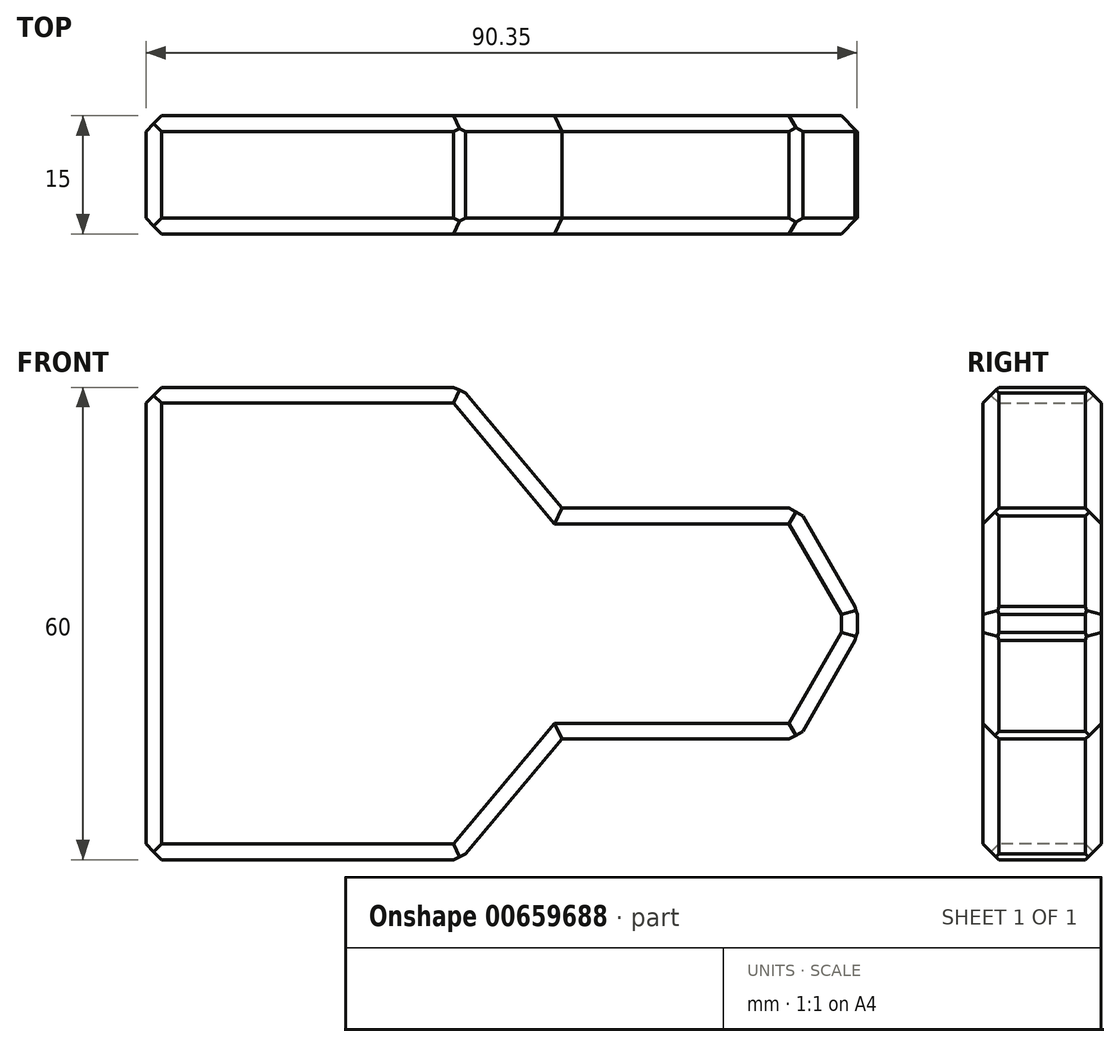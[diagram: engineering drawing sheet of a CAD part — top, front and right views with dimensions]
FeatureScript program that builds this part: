
annotation { "Feature Type Name" : "Feature", "Feature Type Description" : "" }
export const myFeature = defineFeature(function(context is Context, id is Id, definition is map)
    precondition{}
    {
        {
            var Q0;
            Q0=qCreatedBy(makeId("Front.planeOp"),FACE);
            var sketch = newSketch(context, id + "F0", { "sketchPlane" : qUnion([Q0])});
            skLineSegment(sketch, "E0", {"start": v(-70.7, 35.39) * mm, "end": v(-70.7, -24.61) * mm});
            skLineSegment(sketch, "E1", {"start": v(-70.7, -24.61) * mm, "end": v(-30.7, -24.61) * mm});
            skLineSegment(sketch, "E2", {"start": v(-30.7, -24.61) * mm, "end": v(-17.85, -9.3) * mm});
            skLineSegment(sketch, "E3", {"start": v(-17.85, -9.3) * mm, "end": v(12.15, -9.3) * mm});
            skLineSegment(sketch, "E4", {"start": v(12.15, -9.3) * mm, "end": v(19.65, 3.7) * mm});
            skLineSegment(sketch, "E5", {"start": v(-70.7, 35.39) * mm, "end": v(-30.7, 35.39) * mm});
            skLineSegment(sketch, "E6", {"start": v(-30.7, 35.39) * mm, "end": v(-17.85, 20.06) * mm});
            skLineSegment(sketch, "E7", {"start": v(-17.85, 20.06) * mm, "end": v(12.15, 20.06) * mm});
            skLineSegment(sketch, "E8", {"start": v(12.15, 20.06) * mm, "end": v(19.65, 7.07) * mm});
            skLineSegment(sketch, "E9", {"start": v(19.65, 7.07) * mm, "end": v(19.65, 3.7) * mm});
            skSolve(sketch);
        }
        {
            var Q0;
            Q0=makeQuery(id+"F0.imprint","IMPRINT",FACE,{"disambiguationData":[TD([[makeQuery(id+"F0.imprint","IMPRINT",EDGE,{"derivedFrom":sQuery(id+"F0.wireOp",EDGE,"E0")}),1.0]])]});
            extrude(context, id + "F1", {"entities" : qUnion([Q0]), "depth" : 15 * mm, "offsetDistance" : 25 * mm});
        }
        {
            var Q0;
            Q0=makeQuery(id+"F1.opExtrude","CAP_EDGE",EDGE,{"disambiguationData":[OSD([sQuery(id+"F0.wireOp",EDGE,"E5")])],"isStart":false});
            var Q1;
            Q1=makeQuery(id+"F1.opExtrude","CAP_EDGE",EDGE,{"disambiguationData":[OSD([sQuery(id+"F0.wireOp",EDGE,"E6")])],"isStart":false});
            var Q2;
            Q2=makeQuery(id+"F1.opExtrude","CAP_EDGE",EDGE,{"disambiguationData":[OSD([sQuery(id+"F0.wireOp",EDGE,"E7")])],"isStart":false});
            var Q3;
            Q3=makeQuery(id+"F1.opExtrude","CAP_EDGE",EDGE,{"disambiguationData":[OSD([sQuery(id+"F0.wireOp",EDGE,"E8")])],"isStart":false});
            var Q4;
            Q4=makeQuery(id+"F1.opExtrude","CAP_EDGE",EDGE,{"disambiguationData":[OSD([sQuery(id+"F0.wireOp",EDGE,"E4")])],"isStart":false});
            var Q5;
            Q5=makeQuery(id+"F1.opExtrude","CAP_EDGE",EDGE,{"disambiguationData":[OSD([sQuery(id+"F0.wireOp",EDGE,"E9")])],"isStart":false});
            var Q6;
            Q6=makeQuery(id+"F1.opExtrude","CAP_EDGE",EDGE,{"disambiguationData":[OSD([sQuery(id+"F0.wireOp",EDGE,"E3")])],"isStart":false});
            var Q7;
            Q7=makeQuery(id+"F1.opExtrude","CAP_EDGE",EDGE,{"disambiguationData":[OSD([sQuery(id+"F0.wireOp",EDGE,"E2")])],"isStart":false});
            var Q8;
            Q8=makeQuery(id+"F1.opExtrude","CAP_EDGE",EDGE,{"disambiguationData":[OSD([sQuery(id+"F0.wireOp",EDGE,"E1")])],"isStart":false});
            var Q9;
            Q9=makeQuery(id+"F1.opExtrude","CAP_EDGE",EDGE,{"disambiguationData":[OSD([sQuery(id+"F0.wireOp",EDGE,"E0")])],"isStart":false});
            chamfer(context, id + "F2", {"entities" : qUnion([Q0, Q1, Q2, Q3, Q4, Q5, Q6, Q7, Q8, Q9]), "width" : 2 * mm, "tangentPropagation" : true});
        }
        {
            var Q0;
            Q0=makeQuery(id+"F1.opExtrude","CAP_EDGE",EDGE,{"disambiguationData":[OSD([sQuery(id+"F0.wireOp",EDGE,"E5")])],"isStart":true});
            var Q1;
            Q1=makeQuery(id+"F1.opExtrude","CAP_EDGE",EDGE,{"disambiguationData":[OSD([sQuery(id+"F0.wireOp",EDGE,"E0")])],"isStart":true});
            var Q2;
            Q2=makeQuery(id+"F1.opExtrude","CAP_EDGE",EDGE,{"disambiguationData":[OSD([sQuery(id+"F0.wireOp",EDGE,"E1")])],"isStart":true});
            var Q3;
            Q3=makeQuery(id+"F1.opExtrude","CAP_EDGE",EDGE,{"disambiguationData":[OSD([sQuery(id+"F0.wireOp",EDGE,"E2")])],"isStart":true});
            var Q4;
            Q4=makeQuery(id+"F1.opExtrude","CAP_EDGE",EDGE,{"disambiguationData":[OSD([sQuery(id+"F0.wireOp",EDGE,"E3")])],"isStart":true});
            var Q5;
            Q5=makeQuery(id+"F1.opExtrude","CAP_EDGE",EDGE,{"disambiguationData":[OSD([sQuery(id+"F0.wireOp",EDGE,"E4")])],"isStart":true});
            var Q6;
            Q6=makeQuery(id+"F1.opExtrude","CAP_EDGE",EDGE,{"disambiguationData":[OSD([sQuery(id+"F0.wireOp",EDGE,"E9")])],"isStart":true});
            var Q7;
            Q7=makeQuery(id+"F1.opExtrude","CAP_EDGE",EDGE,{"disambiguationData":[OSD([sQuery(id+"F0.wireOp",EDGE,"E8")])],"isStart":true});
            var Q8;
            Q8=makeQuery(id+"F1.opExtrude","CAP_EDGE",EDGE,{"disambiguationData":[OSD([sQuery(id+"F0.wireOp",EDGE,"E7")])],"isStart":true});
            var Q9;
            Q9=makeQuery(id+"F1.opExtrude","CAP_EDGE",EDGE,{"disambiguationData":[OSD([sQuery(id+"F0.wireOp",EDGE,"E6")])],"isStart":true});
            chamfer(context, id + "F3", {"entities" : qUnion([Q0, Q1, Q2, Q3, Q4, Q5, Q6, Q7, Q8, Q9]), "width" : 2 * mm, "tangentPropagation" : true});
        }
        {
            var Q0;
            Q0=makeQuery(id+"F1.opExtrude","SWEPT_EDGE",EDGE,{"disambiguationData":[OSD([sQuery(id+"F0.wireOp",EDGE,"E7"),sQuery(id+"F0.wireOp",EDGE,"E8")])]});
            var Q1;
            Q1=makeQuery(id+"F1.opExtrude","SWEPT_EDGE",EDGE,{"disambiguationData":[OSD([sQuery(id+"F0.wireOp",EDGE,"E8"),sQuery(id+"F0.wireOp",EDGE,"E9")])]});
            var Q2;
            Q2=makeQuery(id+"F1.opExtrude","SWEPT_EDGE",EDGE,{"disambiguationData":[OSD([sQuery(id+"F0.wireOp",EDGE,"E4"),sQuery(id+"F0.wireOp",EDGE,"E9")])]});
            var Q3;
            Q3=makeQuery(id+"F1.opExtrude","SWEPT_EDGE",EDGE,{"disambiguationData":[OSD([sQuery(id+"F0.wireOp",EDGE,"E5"),sQuery(id+"F0.wireOp",EDGE,"E6")])]});
            var Q4;
            Q4=makeQuery(id+"F1.opExtrude","SWEPT_EDGE",EDGE,{"disambiguationData":[OSD([sQuery(id+"F0.wireOp",EDGE,"E0"),sQuery(id+"F0.wireOp",EDGE,"E5")])]});
            var Q5;
            Q5=makeQuery(id+"F1.opExtrude","SWEPT_EDGE",EDGE,{"disambiguationData":[OSD([sQuery(id+"F0.wireOp",EDGE,"E0"),sQuery(id+"F0.wireOp",EDGE,"E1")])]});
            var Q6;
            Q6=makeQuery(id+"F1.opExtrude","SWEPT_EDGE",EDGE,{"disambiguationData":[OSD([sQuery(id+"F0.wireOp",EDGE,"E1"),sQuery(id+"F0.wireOp",EDGE,"E2")])]});
            var Q7;
            Q7=makeQuery(id+"F1.opExtrude","SWEPT_EDGE",EDGE,{"disambiguationData":[OSD([sQuery(id+"F0.wireOp",EDGE,"E3"),sQuery(id+"F0.wireOp",EDGE,"E4")])]});
            chamfer(context, id + "F4", {"entities" : qUnion([Q0, Q1, Q2, Q3, Q4, Q5, Q6, Q7]), "width" : 2 * mm, "tangentPropagation" : true});
        }
    });
